# Revit family: Tap-IntervalTap-Vitra-OtherSeries-A45214
name_source: partatom
category: Plumbing Fixtures
revit_build: Autodesk Revit 2017 (Build: 20160225_1515(x64)
units: mm (PartAtom-declared; Revit-internal decimal feet)

## family parameters
Cut with Voids When Loaded = No
Host = Face
OmniClass Number = 23.45.55.17
OmniClass Title = Mixing Faucets
Part Type = Normal
Room Calculation Point = No
Round Connector Dimension = Use Diameter
Shared = Yes

## types (12) — shared parameters
BIMobject category = Sanitary - Taps & Mixers
CW Connection = Yes
Connection Diameter (mm) = 15 mm  [stored 0.0492126 ft]
Default Elevation = 850 mm  [stored 2.78871 ft]
Description = Interval Tap
Design country = Turkey
HW Connection = Yes
Hot Water Supply (max.) = 80 °C
Hot Water temperature, factory set to = 38 °C
IFC Classification = Sanitary Terminal
Main Material = Brass
Manufacturer = Vitra
Manufacturer name = Vitra
Masterformat 2014 Code = 22 40 00
Masterformat 2014 Description = Plumbing Fixtures
Min. flow pressure of = 0.5 bar
Mounting type = Wall Mounted - Pipe Connect
NBS Referans Code = 31-06
NBS Referans Description = Bathing Fittings
Nominal Depth (mm) = 75 mm
Nominal Height (mm) = 68 mm
Nominal Width (mm) = 60 mm  [stored 0.19685 ft]
Number Of Connections = 1
OmniClass Code = 23-27 31 29
OmniClass Description = Mixing Valves
Product Properties = Energy Saving
Product Type = Angle Stop Valve
Product certification = https://www.vitraglobal.com
Product family = Other
Product group = Angle Stop Valve
Range of Hot Water Supply = 5 - 65 °C
Range of flow pressure = 1 - 5 bar
Test Pressure = 16 bar
UNSPSC Code = 3018
UNSPSC Description = Plumbing fixtures
URL = https://vitraglobal.com
Uniclass 1.4 Code = L725111
Uniclass 1.4 Description = Taps
Uniclass 2.0 Code = PR-31-06
Uniclass 2.0 Description = Bathing Fittings
Uniclass 2015 Code = Pr_40_20_87_09
Uniclass 2015 Name = Bath taps
Uniformat II Code = 22 40 00
Uniformat II Description = Plumbing Fixture
Vent Connection = No
Warranty Period (Year) = 10 Years
Waste Connection = No
Weight Net (kg) = 0.15
Youtube = https://www.youtube.com

## per-type parameters (varying)
| type | Article No. (default) | Brand | Coating Material | Color | Model | Product SKU | Product url | Technical description |
| Tap-IntervalTap-Vitra-OtherSeries-A45214 | A45214 | Artema | Chrome | Chrome | A45214 | A45214 | https://www.vitra.com.tr | https://www.vitra.com.tr |
| Tap-IntervalTap-Vitra-OtherSeries-A4521426 | A4521426 | Artema | BrightCopper | Copper | A4521426 | A4521426 | https://www.vitra.com.tr | https://www.vitra.com.tr |
| Tap-IntervalTap-Vitra-OtherSeries-A4521434 | A4521434 | Artema | Brushed Nickel | Brushed Nickel | A4521434 | A4521434 | https://www.vitra.com.tr | https://www.vitra.com.tr |
| Tap-IntervalTap-Vitra-OtherSeries-A4521436 | A4521436 | Artema | Matte Black | Matte Black | A4521436 | A4521436 | https://www.vitra.com.tr | https://www.vitra.com.tr |
| Tap-IntervalTap-Vitra-OtherSeries-A4521423 | A4521423 | Artema | Gold | Gold | A4521423 | A4521423 | https://www.vitra.com.tr | https://www.vitra.com.tr |
| Tap-IntervalTap-Vitra-OtherSeries-A4521423IND | A4521423IND | VitrA | Gold | Gold | A4521423IND | A4521423IND | https://www.vitra-india.com | https://www.vitra-india.com |
| Tap-IntervalTap-Vitra-OtherSeries-A4521434IND | A4521434IND | VitrA | Brushed Nickel | Brushed Nickel | A4521434IND | A4521434IND | https://www.vitra-india.com | https://www.vitra-india.com |
| Tap-IntervalTap-Vitra-OtherSeries-A4521426IND | A4521426IND | VitrA | BrightCopper | Copper | A4521426IND | A4521426IND | https://www.vitra-india.com | https://www.vitra-india.com |
| Tap-IntervalTap-Vitra-OtherSeries-A4521436IND | A4521436IND | VitrA | Matte Black | Matte Black | A4521436IND | A4521436IND | https://www.vitra-india.com | https://www.vitra-india.com |
| Tap-IntervalTap-Vitra-OtherSeries-A45214EXP | A45214EXP | VitrA | Chrome | Chrome | A45214EXP | A45214EXP | https://www.vitraglobal.com | https://www.vitraglobal.com |
| Tap-IntervalTap-Vitra-OtherSeries-A45214IND | A45214IND | VitrA | Chrome | Chrome | A45214IND | A45214IND | https://www.vitra-india.com | https://www.vitra-india.com |
| Tap-IntervalTap-Vitra-OtherSeries-A45214EKM | A45214EKM | VitrA | Chrome | Chrome | A45214EKM | A45214EKM | https://www.vitra-bad.fr | https://www.vitra-bad.fr |

note: [stored X ft] marks values corroborated as IEEE doubles in the binary element streams (Revit-internal decimal feet)

## geometry (parser evidence)
native form markers: Sweep x2
no freeform markers — native parametric forms only
